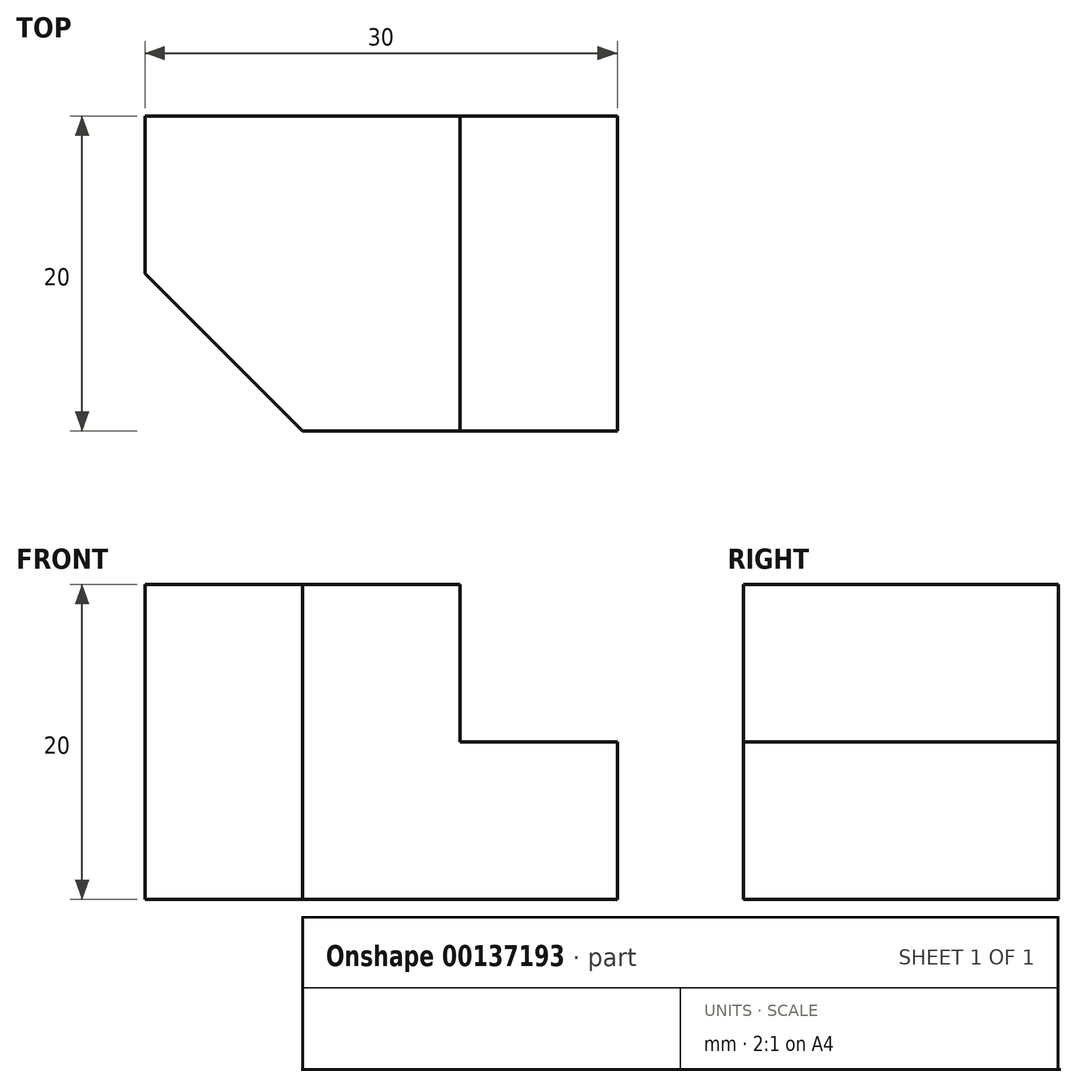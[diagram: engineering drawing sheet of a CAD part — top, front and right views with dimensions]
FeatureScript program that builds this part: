
annotation { "Feature Type Name" : "Feature", "Feature Type Description" : "" }
export const myFeature = defineFeature(function(context is Context, id is Id, definition is map)
    precondition{}
    {
        {
            var Q0;
            Q0=qCreatedBy(makeId("Top.planeOp"),FACE);
            var sketch = newSketch(context, id + "F0", { "sketchPlane" : qUnion([Q0])});
            skLineSegment(sketch, "E0.bottom", {"start": v(0, 0) * mm, "end": v(30, 0) * mm});
            skLineSegment(sketch, "E0.top", {"start": v(0, 20) * mm, "end": v(30, 20) * mm});
            skLineSegment(sketch, "E0.left", {"start": v(0, 0) * mm, "end": v(0, 20) * mm});
            skLineSegment(sketch, "E0.right", {"start": v(30, 0) * mm, "end": v(30, 20) * mm});
            skSolve(sketch);
        }
        {
            var Q0;
            Q0 = qSketchRegion(id + "F0", true);
            extrude(context, id + "F1", {"entities" : qUnion([Q0]), "depth" : 20 * mm});
        }
        {
            var Q0;
            Q0=makeQuery(id+"F1.opExtrude","CAP_FACE",FACE,{"disambiguationData":[OSD([sQuery(id+"F0.wireOp",EDGE,"E0.bottom"),sQuery(id+"F0.wireOp",EDGE,"E0.top"),sQuery(id+"F0.wireOp",EDGE,"E0.left"),sQuery(id+"F0.wireOp",EDGE,"E0.right")])],"isStart":false});
            var sketch = newSketch(context, id + "F2", { "sketchPlane" : qUnion([Q0])});
            skLineSegment(sketch, "E1", {"start": v(0, 0) * mm, "end": v(10, 0) * mm});
            skLineSegment(sketch, "E2", {"start": v(10, 0) * mm, "end": v(0, 10) * mm});
            skLineSegment(sketch, "E3", {"start": v(0, 10) * mm, "end": v(0, 0) * mm});
            skSolve(sketch);
        }
        {
            var Q0;
            Q0 = qSketchRegion(id + "F2", true);
            extrude(context, id + "F3", {"entities" : qUnion([Q0]), "operationType" : NewBodyOperationType.REMOVE, "oppositeDirection" : true, "depth" : 20 * mm});
        }
        {
            var Q0;
            Q0=makeQuery(id+"F1.opExtrude","SWEPT_FACE",FACE,{"disambiguationData":[OSD([sQuery(id+"F0.wireOp",EDGE,"E0.bottom")])]});
            var sketch = newSketch(context, id + "F4", { "sketchPlane" : qUnion([Q0])});
            skLineSegment(sketch, "E4.bottom", {"start": v(30, 20) * mm, "end": v(20, 20) * mm});
            skLineSegment(sketch, "E4.top", {"start": v(30, 10) * mm, "end": v(20, 10) * mm});
            skLineSegment(sketch, "E4.left", {"start": v(30, 20) * mm, "end": v(30, 10) * mm});
            skLineSegment(sketch, "E4.right", {"start": v(20, 20) * mm, "end": v(20, 10) * mm});
            skSolve(sketch);
        }
        {
            var Q0;
            Q0 = qSketchRegion(id + "F4", true);
            extrude(context, id + "F5", {"entities" : qUnion([Q0]), "operationType" : NewBodyOperationType.REMOVE, "oppositeDirection" : true, "depth" : 20 * mm});
        }
    });
